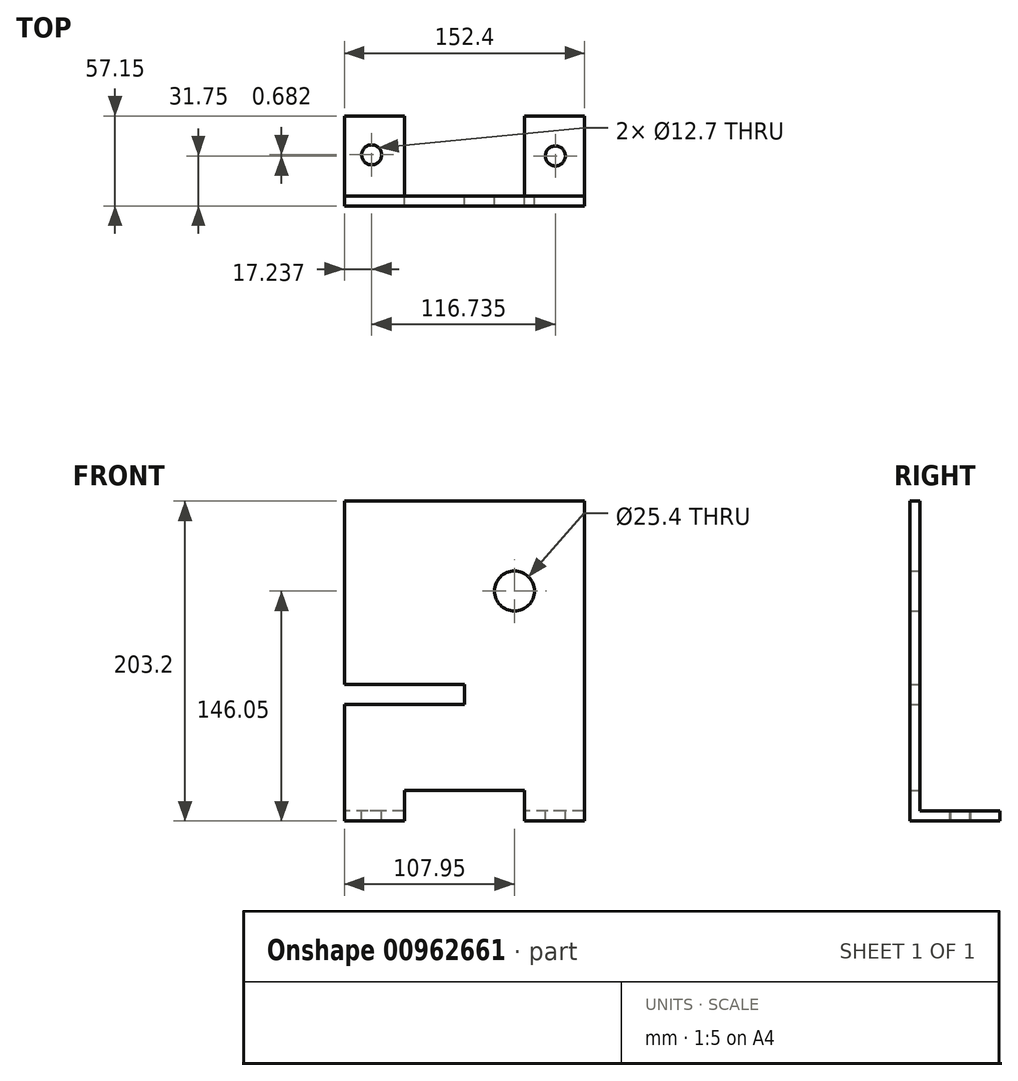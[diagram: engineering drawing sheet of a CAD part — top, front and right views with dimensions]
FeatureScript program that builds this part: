
annotation { "Feature Type Name" : "Feature", "Feature Type Description" : "" }
export const myFeature = defineFeature(function(context is Context, id is Id, definition is map)
    precondition{}
    {
        {
            var Q0;
            Q0=qCreatedBy(makeId("Front.planeOp"),FACE);
            var sketch = newSketch(context, id + "F0", { "sketchPlane" : qUnion([Q0])});
            skCircle(sketch, "E0", {"center": v(0, 0) * mm, "radius": 12.7 * mm});
            skLineSegment(sketch, "E1", {"start": v(-107.95, 57.15) * mm, "end": v(44.45, 57.15) * mm});
            skLineSegment(sketch, "E2", {"start": v(44.45, 57.15) * mm, "end": v(44.45, -146.05) * mm});
            skLineSegment(sketch, "E3", {"start": v(44.45, -146.05) * mm, "end": v(6.35, -146.05) * mm});
            skLineSegment(sketch, "E4", {"start": v(6.35, -146.05) * mm, "end": v(6.35, -126.62) * mm});
            skLineSegment(sketch, "E5", {"start": v(6.35, -126.62) * mm, "end": v(-69.85, -126.62) * mm});
            skLineSegment(sketch, "E6", {"start": v(-69.85, -126.62) * mm, "end": v(-69.85, -146.05) * mm});
            skLineSegment(sketch, "E7", {"start": v(-69.85, -146.05) * mm, "end": v(-107.95, -146.05) * mm});
            skLineSegment(sketch, "E8", {"start": v(-107.95, -146.05) * mm, "end": v(-107.95, -72.09) * mm});
            skLineSegment(sketch, "E9", {"start": v(-107.95, -72.09) * mm, "end": v(-31.62, -72.09) * mm});
            skLineSegment(sketch, "E10", {"start": v(-31.62, -72.09) * mm, "end": v(-31.62, -59.16) * mm});
            skLineSegment(sketch, "E11", {"start": v(-31.62, -59.16) * mm, "end": v(-107.95, -59.16) * mm});
            skLineSegment(sketch, "E12", {"start": v(-107.95, -59.16) * mm, "end": v(-107.95, 57.15) * mm});
            skSolve(sketch);
        }
        {
            var Q0;
            Q0=qSketchRegion(id+"F0",true);
            extrude(context, id + "F1", {"entities" : qUnion([Q0]), "depth" : 6.35 * mm, "offsetDistance" : 25.4 * mm});
        }
        {
            var Q0;
            Q0=makeQuery(id+"F1.opExtrude","CAP_FACE",FACE,{"disambiguationData":[OSD([sQuery(id+"F0.wireOp",EDGE,"E0"),sQuery(id+"F0.wireOp",EDGE,"E1"),sQuery(id+"F0.wireOp",EDGE,"E2"),sQuery(id+"F0.wireOp",EDGE,"E3"),sQuery(id+"F0.wireOp",EDGE,"E4"),sQuery(id+"F0.wireOp",EDGE,"E5"),sQuery(id+"F0.wireOp",EDGE,"E6"),sQuery(id+"F0.wireOp",EDGE,"E7"),sQuery(id+"F0.wireOp",EDGE,"E8"),sQuery(id+"F0.wireOp",EDGE,"E9"),sQuery(id+"F0.wireOp",EDGE,"E10"),sQuery(id+"F0.wireOp",EDGE,"E11"),sQuery(id+"F0.wireOp",EDGE,"E12")])],"isStart":true});
            var sketch = newSketch(context, id + "F2", { "sketchPlane" : qUnion([Q0])});
            skLineSegment(sketch, "E13", {"start": v(-44.45, -139.7) * mm, "end": v(-6.35, -139.7) * mm});
            skLineSegment(sketch, "E14", {"start": v(69.85, -139.7) * mm, "end": v(107.95, -139.7) * mm});
            skSolve(sketch);
        }
        {
            var Q0;
            Q0=qSketchRegion(id+"F2",true);
            var Q1;
            {var subQ0=sQuery(id+"F2.wireOp",EDGE,"E13");Q1=makeQuery(id+"F2.imprint","IMPRINT",FACE,{"disambiguationData":[TD([[makeQuery(id+"F2.imprint","IMPRINT",EDGE,{"derivedFrom":subQ0}),-1.0]])]});}
            var Q2;
            {var subQ0=sQuery(id+"F2.wireOp",EDGE,"E14");Q2=makeQuery(id+"F2.imprint","IMPRINT",FACE,{"disambiguationData":[TD([[makeQuery(id+"F2.imprint","IMPRINT",EDGE,{"derivedFrom":subQ0}),-1.0]])]});}
            extrude(context, id + "F3", {"entities" : qUnion([Q0, Q1, Q2]), "operationType" : NewBodyOperationType.ADD, "depth" : 50.8 * mm, "offsetDistance" : 25.4 * mm});
        }
        {
            var Q0;
            Q0=makeQuery(id+"F3.opExtrude","SWEPT_FACE",FACE,{"disambiguationData":[OSD([sQuery(id+"F2.wireOp",EDGE,"E13")])]});
            var sketch = newSketch(context, id + "F4", { "sketchPlane" : qUnion([Q0])});
            skCircle(sketch, "E15", {"center": v(26.02, 25.4) * mm, "radius": 6.35 * mm});
            skPoint(sketch, "E15.centerSnap0", {"position": v(44.45, 25.4) * mm});
            skCircle(sketch, "E16", {"center": v(-90.71, 26.08) * mm, "radius": 6.35 * mm});
            skSolve(sketch);
        }
        {
            var Q0;
            Q0=qSketchRegion(id+"F4",true);
            extrude(context, id + "F5", {"entities" : qUnion([Q0]), "operationType" : NewBodyOperationType.REMOVE, "oppositeDirection" : true, "depth" : 25.4 * mm, "offsetDistance" : 25.4 * mm});
        }
    });
